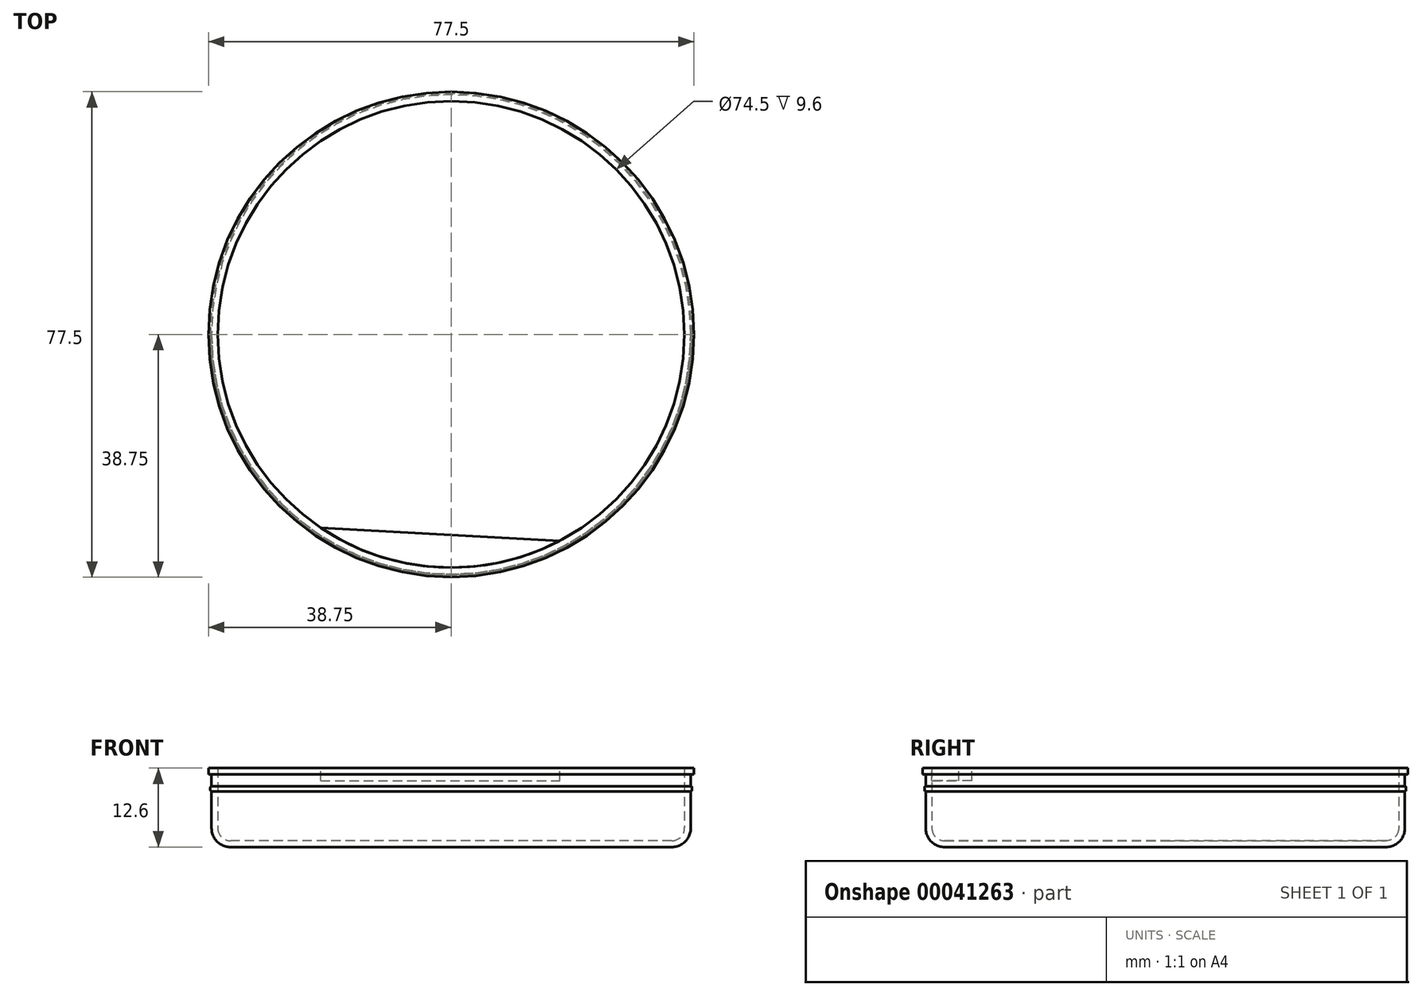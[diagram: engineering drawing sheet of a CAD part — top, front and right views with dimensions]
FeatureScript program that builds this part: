
annotation { "Feature Type Name" : "Feature", "Feature Type Description" : "" }
export const myFeature = defineFeature(function(context is Context, id is Id, definition is map)
    precondition{}
    {
        {
            var Q0;
            Q0=qCreatedBy(makeId("Top.planeOp"),FACE);
            var sketch = newSketch(context, id + "F0", { "sketchPlane" : qUnion([Q0])});
            skCircle(sketch, "E0", {"center": v(0, 0) * mm, "radius": 38.25 * mm});
            skSolve(sketch);
        }
        {
            var Q0;
            Q0 = qSketchRegion(id + "F0", true);
            extrude(context, id + "F1", {"entities" : qUnion([Q0]), "depth" : 11.6 * mm});
        }
        {
            var Q0;
            Q0=makeQuery(id+"F1.opExtrude","CAP_EDGE",EDGE,{"disambiguationData":[OSD([sQuery(id+"F0.wireOp",EDGE,"E0")])],"isStart":true});
            fillet(context, id + "F2", {"entities" : qUnion([Q0]), "radius" : 3 * mm, "tangentPropagation" : true, "allowEdgeOverflow" : false});
        }
        {
            var Q0;
            Q0=makeQuery(id+"F1.opExtrude","CAP_FACE",FACE,{"disambiguationData":[OSD([sQuery(id+"F0.wireOp",EDGE,"E0")])],"isStart":false});
            var sketch = newSketch(context, id + "F3", { "sketchPlane" : qUnion([Q0])});
            skCircle(sketch, "E1", {"center": v(0, 0) * mm, "radius": 38.75 * mm});
            skSolve(sketch);
        }
        {
            var Q0;
            Q0 = qSketchRegion(id + "F3", true);
            extrude(context, id + "F4", {"entities" : qUnion([Q0]), "operationType" : NewBodyOperationType.ADD, "depth" : 1 * mm});
        }
        {
            var Q0;
            Q0=makeQuery(id+"F4.opExtrude","CAP_FACE",FACE,{"disambiguationData":[OSD([sQuery(id+"F3.wireOp",EDGE,"E1")])],"isStart":false});
            shell(context, id + "F5", {"entities" : qUnion([Q0]), "thickness" : 1 * mm});
        }
        {
            var Q0;
            Q0=makeQuery(id+"F4.opExtrude","CAP_FACE",FACE,{"disambiguationData":[OSD([sQuery(id+"F3.wireOp",EDGE,"E1")])],"isStart":false});
            var sketch = newSketch(context, id + "F6", { "sketchPlane" : qUnion([Q0])});
            skLineSegment(sketch, "E2", {"start": v(-20.83, -30.88) * mm, "end": v(17.37, -32.95) * mm});
            skSolve(sketch);
        }
        {
            var Q0;
            {var subQ2=sQuery(id+"F6.wireOp",EDGE,"E2");Q0=makeQuery(id+"F6.imprint","IMPRINT",FACE,{"disambiguationData":[TD([[makeQuery(id+"F6.imprint","IMPRINT",EDGE,{"derivedFrom":subQ2}),-1.0]])]});}
            extrude(context, id + "F7", {"entities" : qUnion([Q0]), "oppositeDirection" : true, "depth" : 2 * mm});
        }
        {
            var Q0;
            Q0=qCreatedBy(makeId("Top.planeOp"),FACE);
            cPlane(context, id + "F8", {"entities" : qUnion([Q0]), "cplaneType" : CPlaneType.OFFSET, "offset" : 3.09 * mm, "width" : 150 * mm, "height" : 150 * mm});
        }
        {
            var Q0;
            Q0=qCreatedBy(id+"F8.planeOp",FACE);
            cPlane(context, id + "F9", {"entities" : qUnion([Q0]), "cplaneType" : CPlaneType.OFFSET, "offset" : 2.85 * mm, "width" : 150 * mm, "height" : 150 * mm});
        }
        {
            var Q0;
            Q0=qCreatedBy(id+"F9.planeOp",FACE);
            cPlane(context, id + "F10", {"entities" : qUnion([Q0]), "cplaneType" : CPlaneType.OFFSET, "offset" : 2.95 * mm, "width" : 150 * mm, "height" : 150 * mm});
        }
        {
            var Q0;
            Q0=qCreatedBy(id+"F10.planeOp",FACE);
            var sketch = newSketch(context, id + "F11", { "sketchPlane" : qUnion([Q0])});
            skLineSegment(sketch, "E3", {"start": v(0, -34.15) * mm, "end": v(0, -66.29) * mm, "construction": true});
            skLineSegment(sketch, "E4.rect.bottom", {"start": v(0.05, -38.44) * mm, "end": v(-0.05, -38.44) * mm});
            skLineSegment(sketch, "E4.rect.top", {"start": v(0.05, -38.25) * mm, "end": v(-0.05, -38.25) * mm});
            skLineSegment(sketch, "E4.rect.left", {"start": v(0.05, -38.44) * mm, "end": v(0.05, -38.25) * mm});
            skLineSegment(sketch, "E4.rect.right", {"start": v(-0.05, -38.44) * mm, "end": v(-0.05, -38.25) * mm});
            skPoint(sketch, "E4.rect.middle", {"position": v(0, -38.35) * mm});
            skSolve(sketch);
        }
        {
            var Q0;
            Q0 = qSketchRegion(id + "F11", true);
            extrude(context, id + "F12", {"entities" : qUnion([Q0]), "operationType" : NewBodyOperationType.ADD, "depth" : .8 * mm});
        }
        {
            var Q0;
            Q0=makeQuery(id+"F12.opExtrude","SWEPT_FACE",FACE,{"disambiguationData":[OSD([sQuery(id+"F11.wireOp",EDGE,"E4.rect.left")])]});
            var Q1;
            {var subQ0=sQuery(id+"F0.wireOp",EDGE,"E0");Q1=makeQuery(id+"F2.opFillet","BLEND_EDGE",EDGE,{"blendedFrom":[makeQuery(id+"F1.opExtrude","CAP_EDGE",EDGE,{"disambiguationData":[OSD([subQ0])],"isStart":true}),makeQuery(id+"F1.opExtrude","SWEPT_FACE",FACE,{"disambiguationData":[OSD([subQ0])]})],"blendedInto":[makeQuery(id+"F1.opExtrude","SWEPT_FACE",FACE,{"disambiguationData":[OSD([subQ0])]})]});}
            revolve(context, id + "F13", {"operationType" : NewBodyOperationType.ADD, "entities" : qUnion([Q0]), "axis" : qUnion([Q1]), "revolveType" : RevolveType.FULL});
        }
        {
            var Q0;
            Q0=makeQuery(id+"F13.opRevolve","SWEPT_FACE",FACE,{"disambiguationData":[OSD([sQuery(id+"F11.wireOp",EDGE,"E4.rect.bottom"),sQuery(id+"F11.wireOp",EDGE,"E4.rect.left")])]});
            var Q1;
            Q1=makeQuery(id+"F12.opExtrude","SWEPT_FACE",FACE,{"disambiguationData":[OSD([sQuery(id+"F11.wireOp",EDGE,"E4.rect.bottom")])]});
            fillet(context, id + "F14", {"entities" : qUnion([Q0, Q1]), "radius" : .2 * mm, "tangentPropagation" : true, "allowEdgeOverflow" : false});
        }
    });
